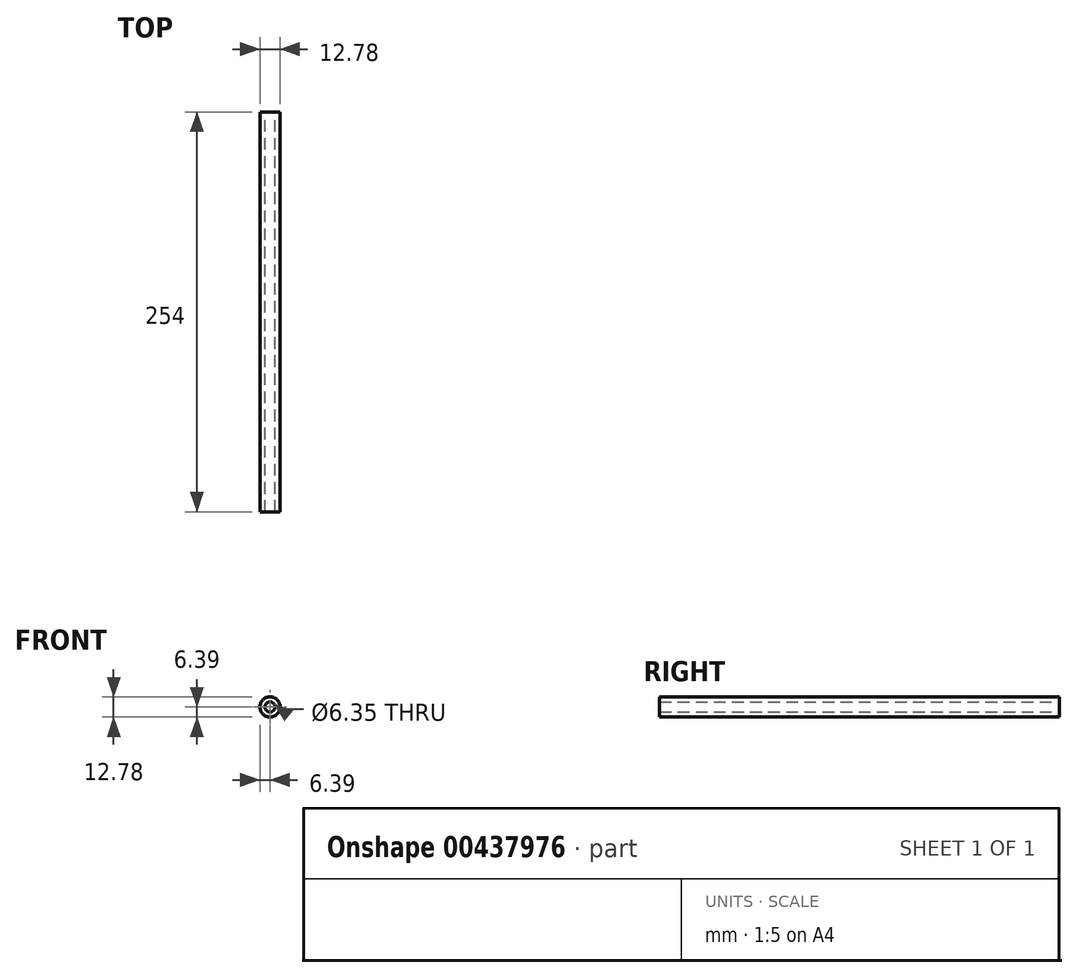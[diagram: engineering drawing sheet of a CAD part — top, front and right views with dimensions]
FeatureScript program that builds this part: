
annotation { "Feature Type Name" : "Feature", "Feature Type Description" : "" }
export const myFeature = defineFeature(function(context is Context, id is Id, definition is map)
    precondition{}
    {
        {
            var Q0;
            Q0=qCreatedBy(makeId("Front.planeOp"),FACE);
            var sketch = newSketch(context, id + "F0", { "sketchPlane" : qUnion([Q0])});
            skCircle(sketch, "E0", {"center": v(0, 0) * mm, "radius": 3.18 * mm});
            skCircle(sketch, "E1", {"center": v(0, 0) * mm, "radius": 6.39 * mm});
            skSolve(sketch);
        }
        {
            var Q0;
            Q0=qSketchRegion(id+"F0",true);
            extrude(context, id + "F1", {"entities" : qUnion([Q0]), "depth" : 25.4 * mm});
        }
        {
            var Q0;
            Q0=qSketchRegion(id+"F0",true);
            extrude(context, id + "F2", {"entities" : qUnion([Q0]), "operationType" : NewBodyOperationType.ADD, "depth" : 254 * mm});
        }
    });
